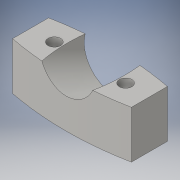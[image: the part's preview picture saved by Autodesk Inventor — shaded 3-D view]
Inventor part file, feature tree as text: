
AUTODESK INVENTOR PART (.ipt)
format: ipt  version: 2016 (Build 200138000, 138)  size: 153,088 bytes
history: native  units: in
note: dims shown in document units (in); Inventor stores cm internally (conversion verified against a paired STEP export)
features: sketch x6, extrude x5, plane x2, hole x1
ambient origin geometry x8: Origin, YZ Plane, XZ Plane, XY Plane, X Axis, Y Axis, Z Axis, Center Point
bodies: Solid1 (feature_tree)
feature tree (14):
  extrude  "Extrusion1"  Depth=1.0in
  hole  "Hole1"  [1 undecoded]
  plane  "Work Plane6"
  extrude  "Extrusion9"  Depth=1.0in
  extrude  "Extrusion5"  Depth=6.5in TaperAngle=0.0deg
  extrude  "Extrusion6"  TaperAngle=90.0deg  [1 undecoded]
  extrude  "Extrusion10"  Depth=6.5in TaperAngle=0.0deg
  sketch  "Sketch1"  dims[d0=2.5in d1=1.0in]
  sketch  "Sketch2"  dims[d2=1.0313in d3=0.0in d4=0.75in]
  sketch  "Sketch6"  dims[d5=0.5in]
  sketch  "Sketch7"  dims[d6=0.266in d7=0.75in d8=0.507in d9=0.25in d10=0.5635in d11=1.0in d12=0.8108in d28=13.0in]
  plane  "Work Plane5"
  sketch  "Sketch10"  dims[d29=6.5in d30=2.0in d31=0.0in]
  sketch  "Sketch11"  dims[d32=6.5in d33=90.0deg d34=2.0in d35=0.0in d48=0.7943in d49=0.1032in d50=1.19in d51=0.19in d52=3.0in d53=0.0in d54=0.0312in d55=0.0in]
note: 2 required parameter values undecoded (feature->parameter linkage not recoverable at this tier; creation-order binding heuristic only, values carry confidence <= 0.55)
